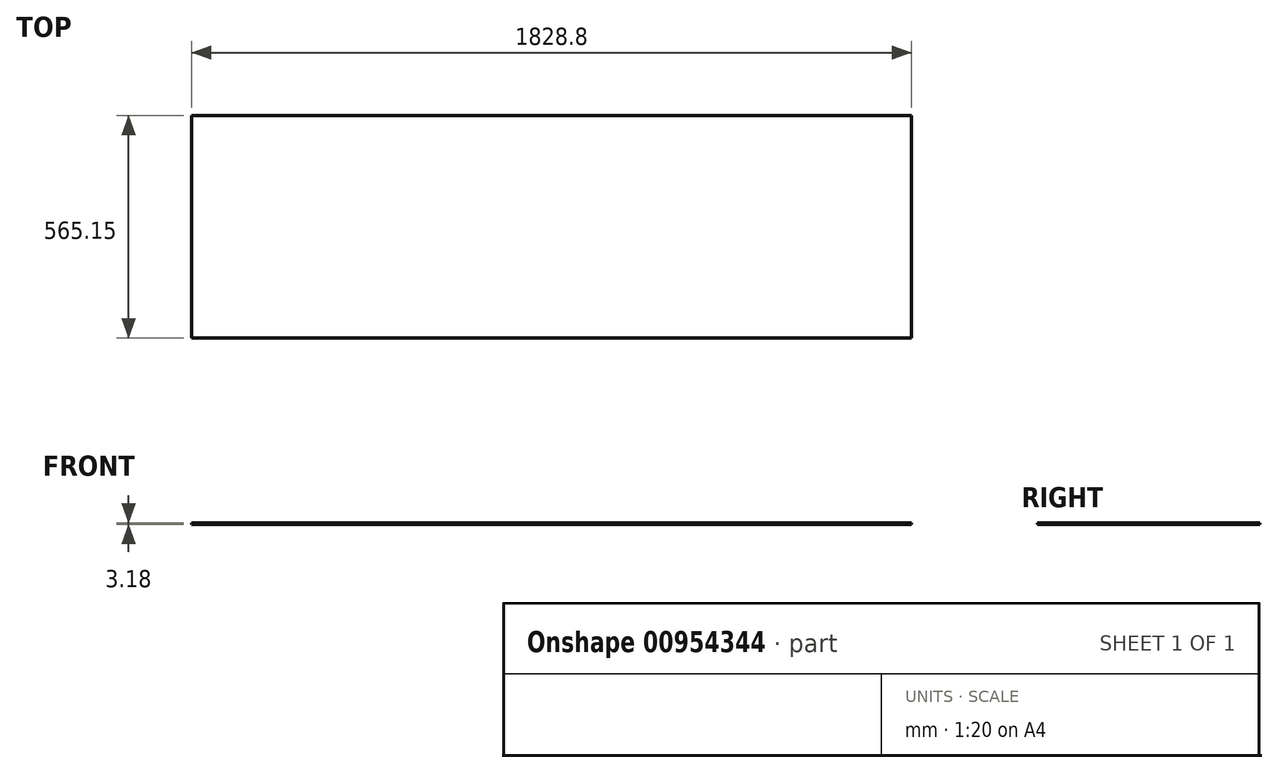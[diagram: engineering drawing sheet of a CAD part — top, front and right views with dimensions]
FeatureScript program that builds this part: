
annotation { "Feature Type Name" : "Feature", "Feature Type Description" : "" }
export const myFeature = defineFeature(function(context is Context, id is Id, definition is map)
    precondition{}
    {
        {
            var Q0;
            Q0=qCreatedBy(makeId("Top.planeOp"),FACE);
            var sketch = newSketch(context, id + "F0", { "sketchPlane" : qUnion([Q0])});
            skLineSegment(sketch, "E0.bottom", {"start": v(-922.62, 299.13) * mm, "end": v(906.18, 299.13) * mm});
            skLineSegment(sketch, "E0.top", {"start": v(-922.62, -266.02) * mm, "end": v(906.18, -266.02) * mm});
            skLineSegment(sketch, "E0.left", {"start": v(-922.62, 299.13) * mm, "end": v(-922.62, -266.02) * mm});
            skLineSegment(sketch, "E0.right", {"start": v(906.18, 299.13) * mm, "end": v(906.18, -266.02) * mm});
            skSolve(sketch);
        }
        {
            var Q0;
            Q0=makeQuery(id+"F0.imprint","IMPRINT",FACE,{"disambiguationData":[TD([[makeQuery(id+"F0.imprint","IMPRINT",EDGE,{"derivedFrom":sQuery(id+"F0.wireOp",EDGE,"E0.bottom")}),-1.0]])]});
            extrude(context, id + "F1", {"entities" : qUnion([Q0]), "depth" : 3.17 * mm, "offsetDistance" : 25.4 * mm, "symmetric" : true});
        }
    });
